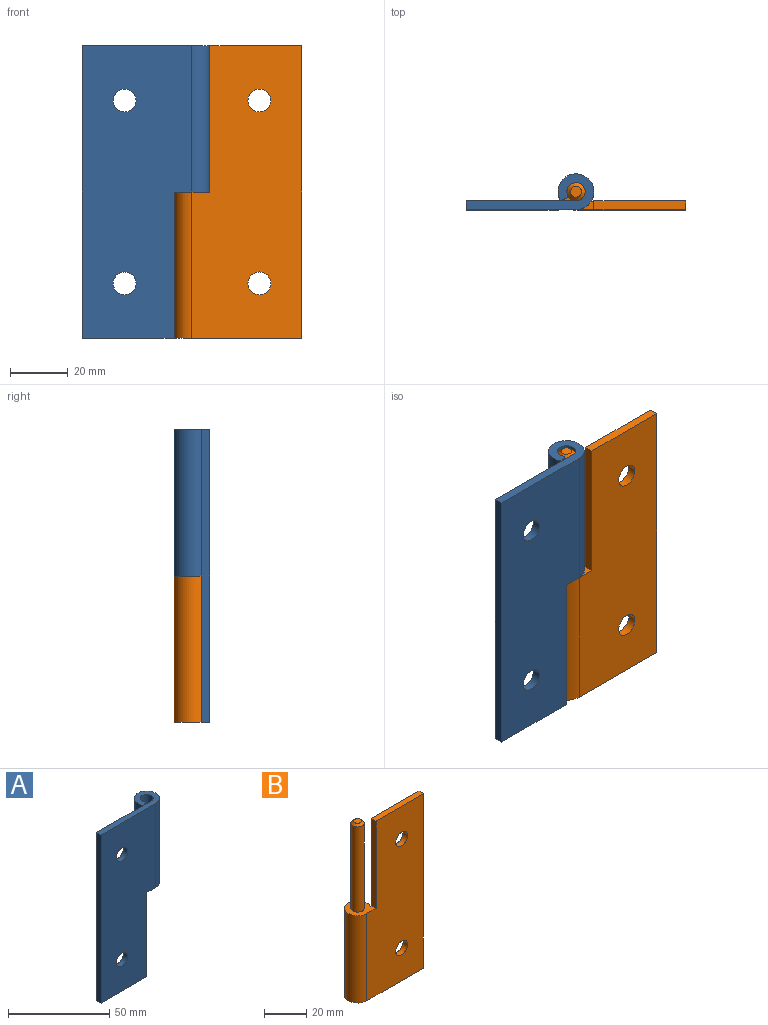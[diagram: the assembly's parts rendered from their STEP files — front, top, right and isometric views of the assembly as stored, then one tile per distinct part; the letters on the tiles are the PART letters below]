
ASSEMBLY  parts=2 mates=1
PART A: 12 faces, bbox 44.3x12.4x101.6 mm
  f0: cylinder r=3.97mm len=7.94mm, axis (0,1,0), area 76mm2, adj f4,f6
  f1: cylinder r=3.97mm len=7.94mm, axis (0,1,0), area 76mm2, adj f4,f6
  f2: cylinder r=3.17mm len=50.8mm, axis (0,0,-1), area 860.4mm2, adj f5,f6,f9,f10
  f3: cylinder r=6.22mm len=50.8mm, axis (0,0,-1), area 1657.5mm2, adj f4,f5,f9,f10
  f4: plane 101.6x38.1mm, normal (0,-1,0), area 3455.9mm2, adj f0,f1,f3,f7,f8,f9,f10,f11
  f5: plane 50.8x2.79mm, normal (0.42,-0.91,0), area 156.2mm2, adj f2,f3,f9,f10
  f6: plane 101.6x38.1mm, normal (0,1,0), area 3455.9mm2, adj f0,f1,f2,f7,f8,f9,f10,f11
  f7: plane 31.88x3.05mm, normal (0,0,-1), area 97.2mm2, adj f4,f6,f8,f11
  f8: plane 101.6x3.05mm, normal (-1,0,0), area 309.7mm2, adj f4,f6,f7,f9
  f9: plane 44.32x12.45mm, normal (0,0,1), area 191.7mm2, adj f2,f3,f4,f5,f6,f8
  f10: plane 12.45x12.45mm, normal (0,0,-1), area 94.5mm2, adj f2,f3,f4,f5,f6,f11
  f11: plane 50.8x3.05mm, normal (1,0,0), area 154.8mm2, adj f4,f6,f7,f10
PART B: 13 faces, bbox 44.3x12.4x101.6 mm
  f0: cylinder r=3.97mm len=7.94mm, axis (0,1,0), area 76mm2, adj f5,f6
  f1: cylinder r=3.97mm len=7.94mm, axis (0,1,0), area 76mm2, adj f5,f6
  f2: cone r=3.17mm half-angle=45deg, axis (0,0,-1), area 28.7mm2, adj f3,f12
  f3: cylinder r=3.17mm len=49.53mm, axis (0,0,-1), area 988.1mm2, adj f2,f10
  f4: cylinder r=6.22mm len=50.8mm, axis (0,0,-1), area 1659mm2, adj f5,f6,f9,f10
  f5: plane 101.6x38.1mm, normal (0,-1,0), area 3455.9mm2, adj f0,f1,f4,f7,f8,f9,f10,f11
  f6: plane 101.6x32.75mm, normal (0,1,0), area 3184mm2, adj f0,f1,f4,f7,f8,f9,f10,f11
  f7: plane 31.88x3.05mm, normal (0,0,1), area 97.2mm2, adj f5,f6,f8,f11
  f8: plane 101.6x3.05mm, normal (1,0,0), area 309.7mm2, adj f5,f6,f7,f9
  f9: plane 44.32x12.45mm, normal (0,0,-1), area 226.2mm2, adj f4,f5,f6,f8
  f10: plane 12.45x12.45mm, normal (0,0,1), area 97.4mm2, adj f3,f4,f5,f6,f11
  f11: plane 50.8x3.05mm, normal (-1,0,0), area 154.8mm2, adj f5,f6,f7,f10
  f12: plane 3.81x3.81mm, normal (0,0,1), area 11.4mm2, adj f2
PLACE A t=(-44.16,-0.85,-57.75)mm
PLACE B t=(-44.16,-0.85,-57.75)mm
MATE revolute B.f2 <-> A.f2  axis (0,0,1) through (-44.16,5.38,-6.95)mm
